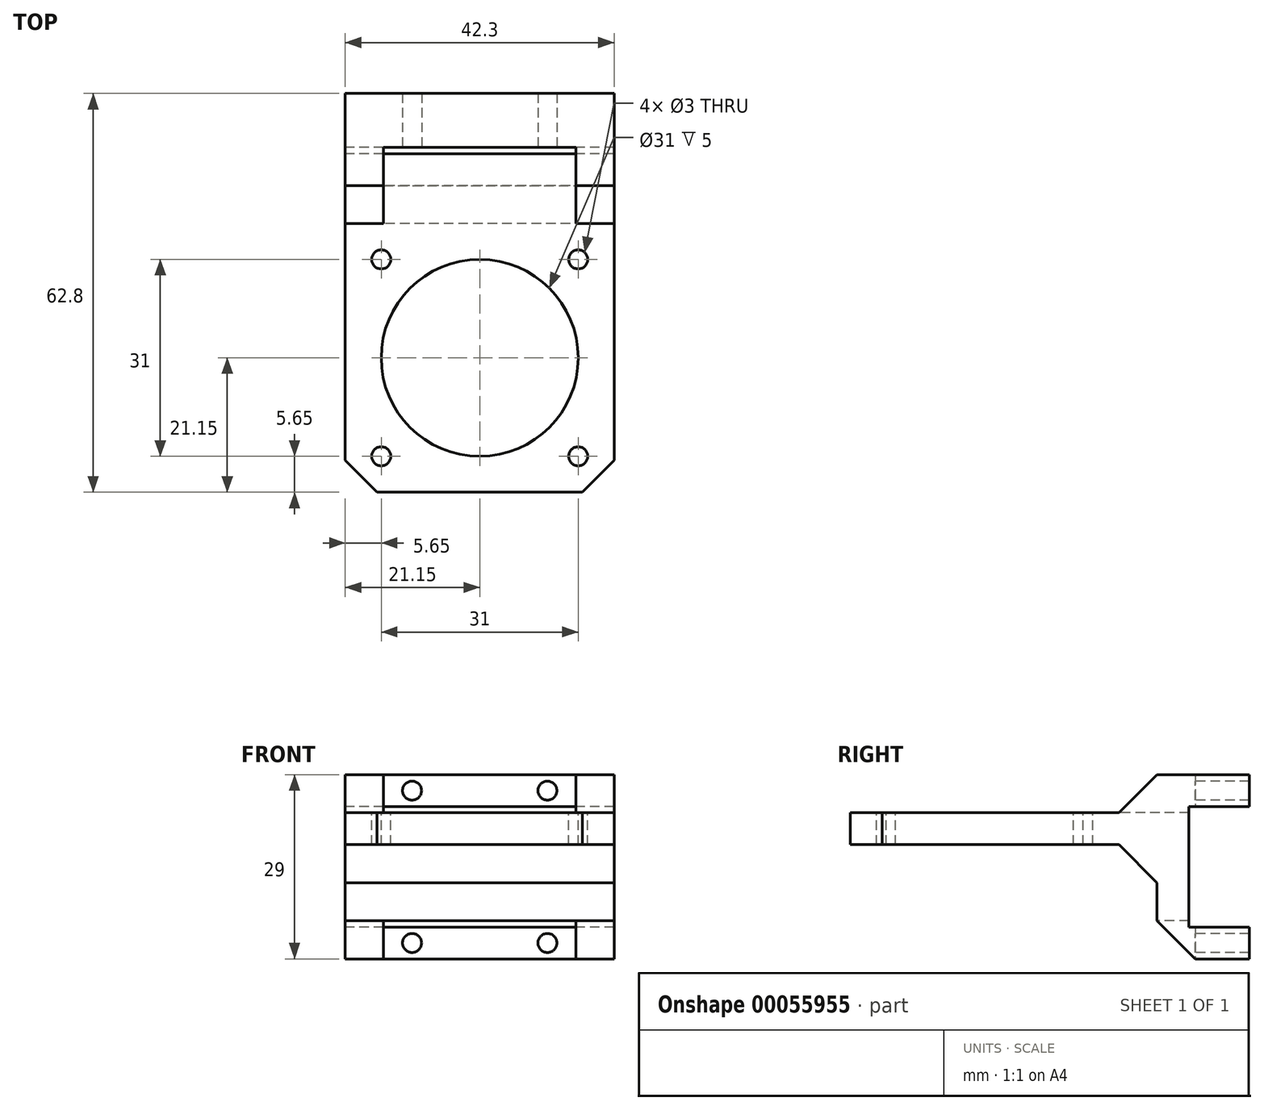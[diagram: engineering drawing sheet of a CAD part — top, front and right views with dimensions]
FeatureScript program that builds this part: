
annotation { "Feature Type Name" : "Feature", "Feature Type Description" : "" }
export const myFeature = defineFeature(function(context is Context, id is Id, definition is map)
    precondition{}
    {
        {
            var Q0;
            Q0=qCreatedBy(makeId("Right.planeOp"),FACE);
            var sketch = newSketch(context, id + "F0", { "sketchPlane" : qUnion([Q0])});
            skLineSegment(sketch, "E0.rect.bottom", {"start": v(0, 9.5) * mm, "end": v(-9.5, 9.5) * mm});
            skLineSegment(sketch, "E0.rect.top", {"start": v(0, -9.5) * mm, "end": v(-9.5, -9.5) * mm});
            skLineSegment(sketch, "E0.rect.right", {"start": v(-9.5, 9.5) * mm, "end": v(-9.5, -9.5) * mm});
            skPoint(sketch, "E0.rect.middle", {"position": v(0, 0) * mm});
            skLineSegment(sketch, "E1.rect.bottom", {"start": v(0, 14.5) * mm, "end": v(-14.5, 14.5) * mm});
            skLineSegment(sketch, "E1.rect.top", {"start": v(0, -14.5) * mm, "end": v(-14.5, -14.5) * mm});
            skLineSegment(sketch, "E2", {"start": v(-14.5, 14.5) * mm, "end": v(-14.5, 8.5) * mm, "construction": true});
            skLineSegment(sketch, "E3", {"start": v(-14.5, 8.5) * mm, "end": v(-14.5, 3.5) * mm, "construction": true});
            skLineSegment(sketch, "E4", {"start": v(-14.5, 3.5) * mm, "end": v(-14.5, -2.5) * mm, "construction": true});
            skLineSegment(sketch, "E5", {"start": v(-14.5, -2.5) * mm, "end": v(-14.5, -14.5) * mm});
            skLineSegment(sketch, "E6.bottom", {"start": v(-14.5, 8.5) * mm, "end": v(-20.5, 8.5) * mm, "construction": true});
            skLineSegment(sketch, "E6.top", {"start": v(-14.5, 3.5) * mm, "end": v(-20.5, 3.5) * mm, "construction": true});
            skLineSegment(sketch, "E6.right", {"start": v(-20.5, 8.5) * mm, "end": v(-20.5, 3.5) * mm, "construction": true});
            skLineSegment(sketch, "E7.bottom", {"start": v(-20.5, 8.5) * mm, "end": v(-62.8, 8.5) * mm});
            skLineSegment(sketch, "E7.top", {"start": v(-20.5, 3.5) * mm, "end": v(-62.8, 3.5) * mm});
            skLineSegment(sketch, "E7.right", {"start": v(-62.8, 8.5) * mm, "end": v(-62.8, 3.5) * mm});
            skLineSegment(sketch, "E8.bottom", {"start": v(-14.5, 14.5) * mm, "end": v(-20.5, 14.5) * mm});
            skLineSegment(sketch, "E8.right", {"start": v(-20.5, 14.5) * mm, "end": v(-20.5, 8.5) * mm});
            skLineSegment(sketch, "E9.bottom", {"start": v(-14.5, -2.5) * mm, "end": v(-20.5, -2.5) * mm});
            skLineSegment(sketch, "E9.right", {"start": v(-20.5, -2.5) * mm, "end": v(-20.5, 3.5) * mm});
            skLineSegment(sketch, "E10", {"start": v(0, 9.5) * mm, "end": v(0, 14.5) * mm});
            skLineSegment(sketch, "E11", {"start": v(0, -9.5) * mm, "end": v(0, -14.5) * mm});
            skSolve(sketch);
        }
        {
            var Q0;
            Q0=makeQuery(id+"F0.imprint","IMPRINT",FACE,{"disambiguationData":[TD([[makeQuery(id+"F0.imprint","IMPRINT",EDGE,{"derivedFrom":sQuery(id+"F0.wireOp",EDGE,"5346ee42-6b44-4ab4-b06a-5ea702be0697.bottom")}),1.0]])]});
            var Q1;
            Q1=makeQuery(id+"F0.imprint","IMPRINT",FACE,{"disambiguationData":[TD([[makeQuery(id+"F0.imprint","IMPRINT",EDGE,{"derivedFrom":sQuery(id+"F0.wireOp",EDGE,"9599e187-f427-41b1-8912-62db417e26b9.bottom")}),1.0]])]});
            var Q2;
            Q2=makeQuery(id+"F0.imprint","IMPRINT",FACE,{"disambiguationData":[TD([[makeQuery(id+"F0.imprint","IMPRINT",EDGE,{"derivedFrom":sQuery(id+"F0.wireOp",EDGE,"E0.rect.bottom")}),-1.0]])]});
            extrude(context, id + "F1", {"entities" : qUnion([Q0, Q1, Q2]), "depth" : 42.3 * mm});
        }
        {
            var Q0;
            Q0=makeQuery(id+"F1.opExtrude","SWEPT_FACE",FACE,{"disambiguationData":[OSD([sQuery(id+"F0.wireOp",EDGE,"E8.right")])]});
            var sketch = newSketch(context, id + "F2", { "sketchPlane" : qUnion([Q0])});
            skLineSegment(sketch, "E12.bottom", {"start": v(0, 14.5) * mm, "end": v(6, 14.5) * mm, "construction": true});
            skLineSegment(sketch, "E12.top", {"start": v(0, 8.5) * mm, "end": v(6, 8.5) * mm, "construction": true});
            skLineSegment(sketch, "E12.left", {"start": v(0, 14.5) * mm, "end": v(0, 8.5) * mm, "construction": true});
            skLineSegment(sketch, "E12.right", {"start": v(6, 14.5) * mm, "end": v(6, 8.5) * mm, "construction": true});
            skLineSegment(sketch, "E13.bottom", {"start": v(42.3, 14.5) * mm, "end": v(36.3, 14.5) * mm, "construction": true});
            skLineSegment(sketch, "E13.top", {"start": v(42.3, 8.5) * mm, "end": v(36.3, 8.5) * mm, "construction": true});
            skLineSegment(sketch, "E13.left", {"start": v(42.3, 14.5) * mm, "end": v(42.3, 8.5) * mm, "construction": true});
            skLineSegment(sketch, "E13.right", {"start": v(36.3, 14.5) * mm, "end": v(36.3, 8.5) * mm, "construction": true});
            skLineSegment(sketch, "E14.bottom", {"start": v(6, 14.5) * mm, "end": v(36.3, 14.5) * mm});
            skLineSegment(sketch, "E14.top", {"start": v(6, 8.5) * mm, "end": v(36.3, 8.5) * mm});
            skLineSegment(sketch, "E14.left", {"start": v(6, 14.5) * mm, "end": v(6, 8.5) * mm});
            skLineSegment(sketch, "E14.right", {"start": v(36.3, 14.5) * mm, "end": v(36.3, 8.5) * mm});
            skSolve(sketch);
        }
        {
            var Q0;
            Q0=makeQuery(id+"F1.opExtrude","SWEPT_FACE",FACE,{"disambiguationData":[OSD([sQuery(id+"F0.wireOp",EDGE,"E5")])]});
            var sketch = newSketch(context, id + "F3", { "sketchPlane" : qUnion([Q0])});
            skLineSegment(sketch, "E15.bottom", {"start": v(0, -14.5) * mm, "end": v(6, -14.5) * mm, "construction": true});
            skLineSegment(sketch, "E15.top", {"start": v(0, -8.5) * mm, "end": v(6, -8.5) * mm, "construction": true});
            skLineSegment(sketch, "E15.left", {"start": v(0, -14.5) * mm, "end": v(0, -8.5) * mm, "construction": true});
            skLineSegment(sketch, "E15.right", {"start": v(6, -14.5) * mm, "end": v(6, -8.5) * mm, "construction": true});
            skLineSegment(sketch, "E16.bottom", {"start": v(42.3, -14.5) * mm, "end": v(36.3, -14.5) * mm, "construction": true});
            skLineSegment(sketch, "E16.top", {"start": v(42.3, -8.54) * mm, "end": v(36.3, -8.54) * mm, "construction": true});
            skLineSegment(sketch, "E16.left", {"start": v(42.3, -14.5) * mm, "end": v(42.3, -8.54) * mm, "construction": true});
            skLineSegment(sketch, "E16.right", {"start": v(36.3, -14.5) * mm, "end": v(36.3, -8.54) * mm, "construction": true});
            skLineSegment(sketch, "E17.bottom", {"start": v(6, -8.5) * mm, "end": v(36.3, -8.5) * mm});
            skLineSegment(sketch, "E17.top", {"start": v(6, -14.5) * mm, "end": v(36.3, -14.5) * mm});
            skLineSegment(sketch, "E17.left", {"start": v(6, -8.5) * mm, "end": v(6, -14.5) * mm});
            skLineSegment(sketch, "E17.right", {"start": v(36.3, -8.5) * mm, "end": v(36.3, -14.5) * mm});
            skSolve(sketch);
        }
        {
            var Q0;
            Q0=makeQuery(id+"F3.imprint","IMPRINT",FACE,{"disambiguationData":[TD([[makeQuery(id+"F3.imprint","IMPRINT",EDGE,{"derivedFrom":sQuery(id+"F3.wireOp",EDGE,"E17.bottom")}),-1.0]])]});
            extrude(context, id + "F4", {"entities" : qUnion([Q0]), "operationType" : NewBodyOperationType.REMOVE, "oppositeDirection" : true, "depth" : 6 * mm});
        }
        {
            var Q0;
            Q0=makeQuery(id+"F2.imprint","IMPRINT",FACE,{"disambiguationData":[TD([[makeQuery(id+"F2.imprint","IMPRINT",EDGE,{"derivedFrom":sQuery(id+"F2.wireOp",EDGE,"E14.bottom")}),1.0]])]});
            extrude(context, id + "F5", {"entities" : qUnion([Q0]), "operationType" : NewBodyOperationType.REMOVE, "oppositeDirection" : true, "depth" : 12 * mm});
        }
        {
            var Q0;
            {var subQ0=sQuery(id+"F0.wireOp",EDGE,"E5");var subQ1=sQuery(id+"F0.wireOp",EDGE,"E1.rect.top");Q0=makeQuery(id+"F4.boolean.opBoolean","SPLIT",EDGE,{"disambiguationData":[TD([makeQuery(id+"F4.opExtrude","SWEPT_FACE",FACE,{"disambiguationData":[OSD([sQuery(id+"F3.wireOp",EDGE,"E17.left")])]})])],"derivedFrom":makeQuery(id+"F1.opExtrude","SWEPT_EDGE",EDGE,{"disambiguationData":[OSD([subQ1,subQ0])]})});}
            var Q1;
            {var subQ0=sQuery(id+"F0.wireOp",EDGE,"E5");var subQ1=sQuery(id+"F0.wireOp",EDGE,"E1.rect.top");Q1=makeQuery(id+"F4.boolean.opBoolean","SPLIT",EDGE,{"disambiguationData":[TD([makeQuery(id+"F4.opExtrude","SWEPT_FACE",FACE,{"disambiguationData":[OSD([sQuery(id+"F3.wireOp",EDGE,"E17.right")])]})])],"derivedFrom":makeQuery(id+"F1.opExtrude","SWEPT_EDGE",EDGE,{"disambiguationData":[OSD([subQ1,subQ0])]})});}
            var Q2;
            {var subQ0=sQuery(id+"F0.wireOp",EDGE,"E5");var subQ1=sQuery(id+"F0.wireOp",EDGE,"E1.rect.top");Q2=makeQuery(id+"F4.boolean.opBoolean","SPLIT",EDGE,{"disambiguationData":[TD([makeQuery(id+"F4.opExtrude","SWEPT_FACE",FACE,{"disambiguationData":[OSD([sQuery(id+"F3.wireOp",EDGE,"E17.left")])]})])],"derivedFrom":makeQuery(id+"F1.opExtrude","SWEPT_EDGE",EDGE,{"disambiguationData":[OSD([subQ1,subQ0])]})});}
            var Q3;
            {var subQ0=sQuery(id+"F0.wireOp",EDGE,"E5");var subQ1=sQuery(id+"F0.wireOp",EDGE,"E1.rect.top");Q3=makeQuery(id+"F4.boolean.opBoolean","SPLIT",EDGE,{"disambiguationData":[TD([makeQuery(id+"F4.opExtrude","SWEPT_FACE",FACE,{"disambiguationData":[OSD([sQuery(id+"F3.wireOp",EDGE,"E17.right")])]})])],"derivedFrom":makeQuery(id+"F1.opExtrude","SWEPT_EDGE",EDGE,{"disambiguationData":[OSD([subQ1,subQ0])]})});}
            var Q4;
            {var subQ0=sQuery(id+"F0.wireOp",EDGE,"E8.right");var subQ1=sQuery(id+"F0.wireOp",EDGE,"E8.bottom");Q4=makeQuery(id+"F5.boolean.opBoolean","SPLIT",EDGE,{"disambiguationData":[TD([makeQuery(id+"F5.opExtrude","SWEPT_FACE",FACE,{"disambiguationData":[OSD([sQuery(id+"F2.wireOp",EDGE,"E14.left")])]})])],"derivedFrom":makeQuery(id+"F1.opExtrude","SWEPT_EDGE",EDGE,{"disambiguationData":[OSD([subQ1,subQ0])]})});}
            var Q5;
            {var subQ0=sQuery(id+"F0.wireOp",EDGE,"E8.right");var subQ1=sQuery(id+"F0.wireOp",EDGE,"E8.bottom");Q5=makeQuery(id+"F5.boolean.opBoolean","SPLIT",EDGE,{"disambiguationData":[TD([makeQuery(id+"F5.opExtrude","SWEPT_FACE",FACE,{"disambiguationData":[OSD([sQuery(id+"F2.wireOp",EDGE,"E14.right")])]})])],"derivedFrom":makeQuery(id+"F1.opExtrude","SWEPT_EDGE",EDGE,{"disambiguationData":[OSD([subQ1,subQ0])]})});}
            var Q6;
            Q6=makeQuery(id+"F1.opExtrude","SWEPT_EDGE",EDGE,{"disambiguationData":[OSD([sQuery(id+"F0.wireOp",EDGE,"E9.bottom"),sQuery(id+"F0.wireOp",EDGE,"E9.right")])]});
            var Q7;
            {var subQ0=sQuery(id+"F0.wireOp",EDGE,"E5");var subQ1=sQuery(id+"F0.wireOp",EDGE,"E1.rect.top");Q7=makeQuery(id+"F4.boolean.opBoolean","SPLIT",EDGE,{"disambiguationData":[TD([makeQuery(id+"F4.opExtrude","SWEPT_FACE",FACE,{"disambiguationData":[OSD([sQuery(id+"F3.wireOp",EDGE,"E17.left")])]})])],"derivedFrom":makeQuery(id+"F1.opExtrude","SWEPT_EDGE",EDGE,{"disambiguationData":[OSD([subQ1,subQ0])]})});}
            var Q8;
            {var subQ0=sQuery(id+"F0.wireOp",EDGE,"E5");var subQ1=sQuery(id+"F0.wireOp",EDGE,"E1.rect.top");Q8=makeQuery(id+"F4.boolean.opBoolean","SPLIT",EDGE,{"disambiguationData":[TD([makeQuery(id+"F4.opExtrude","SWEPT_FACE",FACE,{"disambiguationData":[OSD([sQuery(id+"F3.wireOp",EDGE,"E17.right")])]})])],"derivedFrom":makeQuery(id+"F1.opExtrude","SWEPT_EDGE",EDGE,{"disambiguationData":[OSD([subQ1,subQ0])]})});}
            var Q9;
            {var subQ0=sQuery(id+"F0.wireOp",EDGE,"E5");var subQ1=sQuery(id+"F0.wireOp",EDGE,"E1.rect.top");Q9=makeQuery(id+"F4.boolean.opBoolean","SPLIT",EDGE,{"disambiguationData":[TD([makeQuery(id+"F4.opExtrude","SWEPT_FACE",FACE,{"disambiguationData":[OSD([sQuery(id+"F3.wireOp",EDGE,"E17.left")])]})])],"derivedFrom":makeQuery(id+"F1.opExtrude","SWEPT_EDGE",EDGE,{"disambiguationData":[OSD([subQ1,subQ0])]})});}
            var Q10;
            {var subQ0=sQuery(id+"F0.wireOp",EDGE,"E5");var subQ1=sQuery(id+"F0.wireOp",EDGE,"E1.rect.top");Q10=makeQuery(id+"F4.boolean.opBoolean","SPLIT",EDGE,{"disambiguationData":[TD([makeQuery(id+"F4.opExtrude","SWEPT_FACE",FACE,{"disambiguationData":[OSD([sQuery(id+"F3.wireOp",EDGE,"E17.right")])]})])],"derivedFrom":makeQuery(id+"F1.opExtrude","SWEPT_EDGE",EDGE,{"disambiguationData":[OSD([subQ1,subQ0])]})});}
            chamfer(context, id + "F6", {"entities" : qUnion([Q0, Q1, Q2, Q3, Q4, Q5, Q6, Q7, Q8, Q9, Q10]), "width" : 6 * mm, "tangentPropagation" : true});
        }
        {
            var Q0;
            Q0=makeQuery(id+"F5.boolean.opBoolean","COPY",FACE,{"derivedFrom":makeQuery(id+"F5.opExtrude","CAP_FACE",FACE,{"disambiguationData":[OSD([sQuery(id+"F2.wireOp",EDGE,"E14.bottom"),sQuery(id+"F2.wireOp",EDGE,"E14.top"),sQuery(id+"F2.wireOp",EDGE,"E14.left"),sQuery(id+"F2.wireOp",EDGE,"E14.right")])],"isStart":false})});
            var sketch = newSketch(context, id + "F7", { "sketchPlane" : qUnion([Q0])});
            skLineSegment(sketch, "E18.bottom", {"start": v(6, 14.5) * mm, "end": v(8, 14.5) * mm, "construction": true});
            skLineSegment(sketch, "E18.top", {"start": v(6, 9.5) * mm, "end": v(8, 9.5) * mm, "construction": true});
            skLineSegment(sketch, "E18.left", {"start": v(6, 14.5) * mm, "end": v(6, 9.5) * mm, "construction": true});
            skLineSegment(sketch, "E18.right", {"start": v(8, 14.5) * mm, "end": v(8, 9.5) * mm, "construction": true});
            skLineSegment(sketch, "E19.bottom", {"start": v(36.3, 14.5) * mm, "end": v(34.3, 14.5) * mm, "construction": true});
            skLineSegment(sketch, "E19.top", {"start": v(36.3, 9.5) * mm, "end": v(34.3, 9.5) * mm, "construction": true});
            skLineSegment(sketch, "E19.left", {"start": v(36.3, 14.5) * mm, "end": v(36.3, 9.5) * mm, "construction": true});
            skLineSegment(sketch, "E19.right", {"start": v(34.3, 14.5) * mm, "end": v(34.3, 9.5) * mm, "construction": true});
            skLineSegment(sketch, "E20.bottom", {"start": v(8, 14.5) * mm, "end": v(13, 14.5) * mm, "construction": true});
            skLineSegment(sketch, "E20.top", {"start": v(8, 9.5) * mm, "end": v(13, 9.5) * mm, "construction": true});
            skLineSegment(sketch, "E20.right", {"start": v(13, 14.5) * mm, "end": v(13, 9.5) * mm, "construction": true});
            skLineSegment(sketch, "E21.bottom", {"start": v(34.3, 14.5) * mm, "end": v(29.3, 14.5) * mm, "construction": true});
            skLineSegment(sketch, "E21.top", {"start": v(34.3, 9.5) * mm, "end": v(29.3, 9.5) * mm, "construction": true});
            skLineSegment(sketch, "E21.right", {"start": v(29.3, 14.5) * mm, "end": v(29.3, 9.5) * mm, "construction": true});
            skLineSegment(sketch, "E22", {"start": v(8, 14.5) * mm, "end": v(13, 9.5) * mm, "construction": true});
            skLineSegment(sketch, "E23", {"start": v(29.3, 14.5) * mm, "end": v(34.3, 9.5) * mm, "construction": true});
            skCircle(sketch, "E24", {"center": v(10.5, 12) * mm, "radius": 1.5 * mm});
            skCircle(sketch, "E25", {"center": v(31.8, 12) * mm, "radius": 1.5 * mm});
            skSolve(sketch);
        }
        {
            var Q0;
            Q0=makeQuery(id+"F7.imprint","IMPRINT",FACE,{"disambiguationData":[TD([[makeQuery(id+"F7.imprint","IMPRINT",EDGE,{"derivedFrom":sQuery(id+"F7.wireOp",EDGE,"E24")}),1.0]])]});
            var Q1;
            Q1=makeQuery(id+"F7.imprint","IMPRINT",FACE,{"disambiguationData":[TD([[makeQuery(id+"F7.imprint","IMPRINT",EDGE,{"derivedFrom":sQuery(id+"F7.wireOp",EDGE,"E25")}),1.0]])]});
            extrude(context, id + "F8", {"entities" : qUnion([Q0, Q1]), "operationType" : NewBodyOperationType.REMOVE, "endBound" : BoundingType.THROUGH_ALL, "oppositeDirection" : true, "depth" : 25 * mm});
        }
        {
            var Q0;
            Q0=makeQuery(id+"F4.boolean.opBoolean","COPY",FACE,{"derivedFrom":makeQuery(id+"F4.opExtrude","CAP_FACE",FACE,{"disambiguationData":[OSD([sQuery(id+"F3.wireOp",EDGE,"E17.bottom"),sQuery(id+"F3.wireOp",EDGE,"E17.top"),sQuery(id+"F3.wireOp",EDGE,"E17.left"),sQuery(id+"F3.wireOp",EDGE,"E17.right")])],"isStart":false})});
            var sketch = newSketch(context, id + "F9", { "sketchPlane" : qUnion([Q0])});
            skLineSegment(sketch, "E26", {"start": v(6, -9.5) * mm, "end": v(8, -9.5) * mm, "construction": true});
            skLineSegment(sketch, "E27", {"start": v(8, -9.5) * mm, "end": v(13, -9.5) * mm, "construction": true});
            skLineSegment(sketch, "E28", {"start": v(36.3, -9.5) * mm, "end": v(34.3, -9.5) * mm, "construction": true});
            skLineSegment(sketch, "E29", {"start": v(34.3, -9.5) * mm, "end": v(29.3, -9.5) * mm, "construction": true});
            skLineSegment(sketch, "E30", {"start": v(8, -9.5) * mm, "end": v(13, -14.5) * mm, "construction": true});
            skLineSegment(sketch, "E31", {"start": v(29.3, -9.5) * mm, "end": v(34.3, -14.5) * mm, "construction": true});
            skCircle(sketch, "E32", {"center": v(10.5, -12) * mm, "radius": 1.5 * mm});
            skCircle(sketch, "E33", {"center": v(31.8, -12) * mm, "radius": 1.5 * mm});
            skSolve(sketch);
        }
        {
            var Q0;
            Q0=makeQuery(id+"F9.imprint","IMPRINT",FACE,{"disambiguationData":[TD([[makeQuery(id+"F9.imprint","IMPRINT",EDGE,{"derivedFrom":sQuery(id+"F9.wireOp",EDGE,"E32")}),1.0]])]});
            var Q1;
            Q1=makeQuery(id+"F9.imprint","IMPRINT",FACE,{"disambiguationData":[TD([[makeQuery(id+"F9.imprint","IMPRINT",EDGE,{"derivedFrom":sQuery(id+"F9.wireOp",EDGE,"E33")}),1.0]])]});
            extrude(context, id + "F10", {"entities" : qUnion([Q0, Q1]), "operationType" : NewBodyOperationType.REMOVE, "endBound" : BoundingType.THROUGH_ALL, "oppositeDirection" : true, "depth" : 25 * mm});
        }
        {
            var Q0;
            Q0=makeQuery(id+"F5.boolean.opBoolean","MERGE",FACE,{"derivedFrom":[makeQuery(id+"F1.opExtrude","SWEPT_FACE",FACE,{"disambiguationData":[OSD([sQuery(id+"F0.wireOp",EDGE,"E7.bottom")])]}),makeQuery(id+"F5.opExtrude","SWEPT_FACE",FACE,{"disambiguationData":[OSD([sQuery(id+"F2.wireOp",EDGE,"E14.top")])]})]});
            var sketch = newSketch(context, id + "F11", { "sketchPlane" : qUnion([Q0])});
            skLineSegment(sketch, "E34", {"start": v(42.3, -62.8) * mm, "end": v(0, -20.5) * mm, "construction": true});
            skCircle(sketch, "E35", {"center": v(21.15, -41.65) * mm, "radius": 15.5 * mm});
            skLineSegment(sketch, "E36.rect.bottom", {"start": v(36.65, -26.15) * mm, "end": v(5.65, -26.15) * mm, "construction": true});
            skLineSegment(sketch, "E36.rect.top", {"start": v(36.65, -57.15) * mm, "end": v(5.65, -57.15) * mm, "construction": true});
            skLineSegment(sketch, "E36.rect.left", {"start": v(36.65, -26.15) * mm, "end": v(36.65, -57.15) * mm, "construction": true});
            skLineSegment(sketch, "E36.rect.right", {"start": v(5.65, -26.15) * mm, "end": v(5.65, -57.15) * mm, "construction": true});
            skCircle(sketch, "E37", {"center": v(5.65, -26.15) * mm, "radius": 1.5 * mm});
            skCircle(sketch, "E38", {"center": v(36.65, -26.15) * mm, "radius": 1.5 * mm});
            skCircle(sketch, "E39", {"center": v(36.65, -57.15) * mm, "radius": 1.5 * mm});
            skCircle(sketch, "E40", {"center": v(5.65, -57.15) * mm, "radius": 1.5 * mm});
            skSolve(sketch);
        }
        {
            var Q0;
            Q0=makeQuery(id+"F11.imprint","IMPRINT",FACE,{"disambiguationData":[TD([[makeQuery(id+"F11.imprint","IMPRINT",EDGE,{"derivedFrom":sQuery(id+"F11.wireOp",EDGE,"E40")}),1.0]])]});
            var Q1;
            Q1=makeQuery(id+"F11.imprint","IMPRINT",FACE,{"disambiguationData":[TD([[makeQuery(id+"F11.imprint","IMPRINT",EDGE,{"derivedFrom":sQuery(id+"F11.wireOp",EDGE,"E37")}),1.0]])]});
            var Q2;
            Q2=makeQuery(id+"F11.imprint","IMPRINT",FACE,{"disambiguationData":[TD([[makeQuery(id+"F11.imprint","IMPRINT",EDGE,{"derivedFrom":sQuery(id+"F11.wireOp",EDGE,"E38")}),1.0]])]});
            var Q3;
            Q3=makeQuery(id+"F11.imprint","IMPRINT",FACE,{"disambiguationData":[TD([[makeQuery(id+"F11.imprint","IMPRINT",EDGE,{"derivedFrom":sQuery(id+"F11.wireOp",EDGE,"E39")}),1.0]])]});
            var Q4;
            Q4=makeQuery(id+"F11.imprint","IMPRINT",FACE,{"disambiguationData":[TD([[makeQuery(id+"F11.imprint","IMPRINT",EDGE,{"derivedFrom":sQuery(id+"F11.wireOp",EDGE,"E35")}),1.0]])]});
            extrude(context, id + "F12", {"entities" : qUnion([Q0, Q1, Q2, Q3, Q4]), "operationType" : NewBodyOperationType.REMOVE, "endBound" : BoundingType.UP_TO_NEXT, "oppositeDirection" : true, "depth" : 25 * mm});
        }
        {
            var Q0;
            Q0=makeQuery(id+"F1.opExtrude","CAP_EDGE",EDGE,{"disambiguationData":[OSD([sQuery(id+"F0.wireOp",EDGE,"E7.right")])],"isStart":false});
            var Q1;
            Q1=makeQuery(id+"F1.opExtrude","CAP_EDGE",EDGE,{"disambiguationData":[OSD([sQuery(id+"F0.wireOp",EDGE,"E7.right")])],"isStart":true});
            chamfer(context, id + "F13", {"entities" : qUnion([Q0, Q1]), "width" : 5 * mm, "tangentPropagation" : true});
        }
    });
